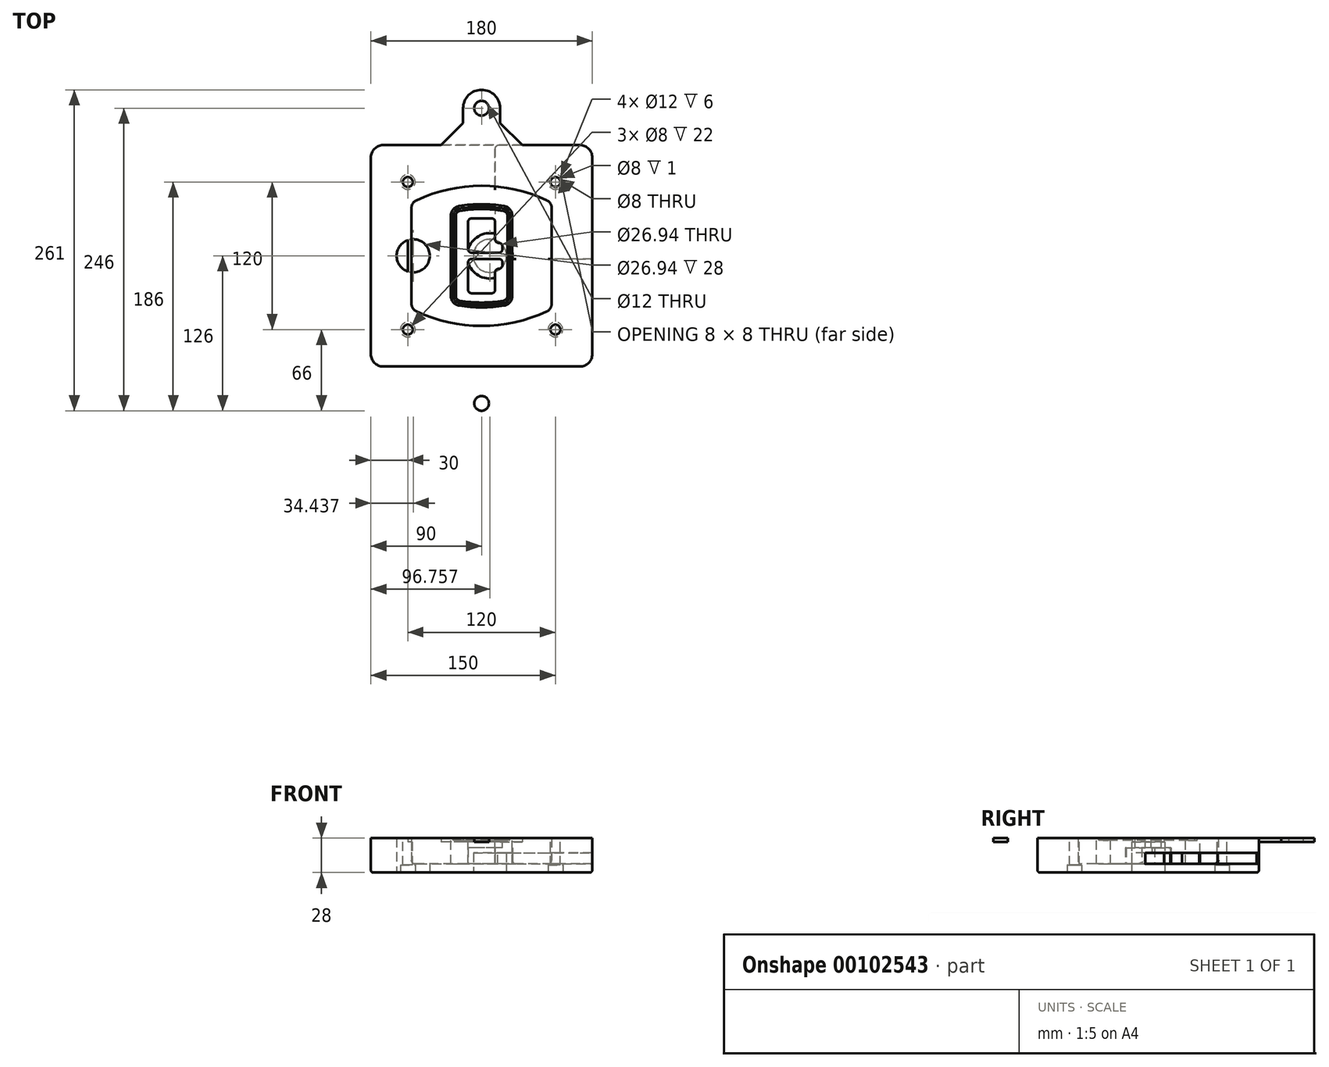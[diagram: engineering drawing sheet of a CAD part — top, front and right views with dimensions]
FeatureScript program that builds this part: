
annotation { "Feature Type Name" : "Feature", "Feature Type Description" : "" }
export const myFeature = defineFeature(function(context is Context, id is Id, definition is map)
    precondition{}
    {
        {
            var Q0;
            Q0=qCreatedBy(makeId("Top.planeOp"),FACE);
            var sketch = newSketch(context, id + "F0", { "sketchPlane" : qUnion([Q0])});
            skPoint(sketch, "E0.rect.middle", {"position": v(0, 0) * mm});
            skLineSegment(sketch, "E1.bottom", {"start": v(-80, -90) * mm, "end": v(80, -90) * mm});
            skLineSegment(sketch, "E1.top", {"start": v(-80, 90) * mm, "end": v(80, 90) * mm});
            skLineSegment(sketch, "E1.left", {"start": v(-90, -80) * mm, "end": v(-90, 80) * mm});
            skLineSegment(sketch, "E1.right", {"start": v(90, -80) * mm, "end": v(90, 80) * mm});
            skLineSegment(sketch, "E2", {"start": v(-90, 90) * mm, "end": v(90, -90) * mm, "construction": true});
            skLineSegment(sketch, "E3", {"start": v(90, 90) * mm, "end": v(-90, -90) * mm, "construction": true});
            skCircle(sketch, "E4", {"center": v(-60, 60) * mm, "radius": 4 * mm});
            skCircle(sketch, "E5", {"center": v(60, 60) * mm, "radius": 4 * mm});
            skCircle(sketch, "E6", {"center": v(60, -60) * mm, "radius": 4 * mm});
            skCircle(sketch, "E7", {"center": v(-60, -60) * mm, "radius": 4 * mm});
            skLineSegment(sketch, "E8", {"start": v(-60, 60) * mm, "end": v(60, 60) * mm, "construction": true});
            skLineSegment(sketch, "E9", {"start": v(60, 60) * mm, "end": v(60, -60) * mm, "construction": true});
            skLineSegment(sketch, "E10", {"start": v(60, -60) * mm, "end": v(-60, -60) * mm, "construction": true});
            skLineSegment(sketch, "E11", {"start": v(-60, -60) * mm, "end": v(-60, 60) * mm, "construction": true});
            skLineSegment(sketch, "E12", {"start": v(-60, 38.83) * mm, "end": v(-60, -38.83) * mm});
            skLineSegment(sketch, "E13", {"start": v(60, 38.83) * mm, "end": v(60, -38.83) * mm});
            skArc(sketch, "E14", {"start": v(54.26, 47.88) * mm, "mid": v(0, 60) * mm, "end": v(-54.26, 47.88) * mm});
            skArc(sketch, "E15", {"start": v(-54.26, -47.88) * mm, "mid": v(0, -60) * mm, "end": v(54.26, -47.88) * mm});
            skLineSegment(sketch, "E16", {"start": v(-60, 0) * mm, "end": v(60, 0) * mm, "construction": true});
            skPoint(sketch, "E17.visualSharp", {"position": v(-60, -45) * mm});
            skArc(sketch, "E17.filletArc", {"start": v(-60, -38.83) * mm, "mid": v(-58.44, -44.2) * mm, "end": v(-54.26, -47.88) * mm});
            skPoint(sketch, "E18.visualSharp", {"position": v(-60, 45) * mm});
            skArc(sketch, "E18.filletArc", {"start": v(-54.26, 47.88) * mm, "mid": v(-58.44, 44.2) * mm, "end": v(-60, 38.83) * mm});
            skPoint(sketch, "E19.visualSharp", {"position": v(60, 45) * mm});
            skArc(sketch, "E19.filletArc", {"start": v(60, 38.83) * mm, "mid": v(58.44, 44.2) * mm, "end": v(54.26, 47.88) * mm});
            skPoint(sketch, "E20.visualSharp", {"position": v(60, -45) * mm});
            skArc(sketch, "E20.filletArc", {"start": v(54.26, -47.88) * mm, "mid": v(58.44, -44.2) * mm, "end": v(60, -38.83) * mm});
            skPoint(sketch, "E21.visualSharp", {"position": v(-90, 90) * mm});
            skArc(sketch, "E21.filletArc", {"start": v(-80, 90) * mm, "mid": v(-87.07, 87.07) * mm, "end": v(-90, 80) * mm});
            skPoint(sketch, "E22.visualSharp", {"position": v(90, 90) * mm});
            skArc(sketch, "E22.filletArc", {"start": v(90, 80) * mm, "mid": v(87.07, 87.07) * mm, "end": v(80, 90) * mm});
            skPoint(sketch, "E23.visualSharp", {"position": v(90, -90) * mm});
            skArc(sketch, "E23.filletArc", {"start": v(80, -90) * mm, "mid": v(87.07, -87.07) * mm, "end": v(90, -80) * mm});
            skPoint(sketch, "E24.visualSharp", {"position": v(-90, -90) * mm});
            skArc(sketch, "E24.filletArc", {"start": v(-90, -80) * mm, "mid": v(-87.07, -87.07) * mm, "end": v(-80, -90) * mm});
            skArc(sketch, "E25.0", {"start": v(57, 38.83) * mm, "mid": v(55.9, 42.58) * mm, "end": v(52.98, 45.17) * mm});
            skLineSegment(sketch, "E25.1", {"start": v(57, 38.83) * mm, "end": v(57, -38.83) * mm});
            skArc(sketch, "E25.2", {"start": v(52.98, -45.17) * mm, "mid": v(55.9, -42.58) * mm, "end": v(57, -38.83) * mm});
            skArc(sketch, "E25.3", {"start": v(-52.98, -45.17) * mm, "mid": v(0, -57) * mm, "end": v(52.98, -45.17) * mm});
            skArc(sketch, "E25.4", {"start": v(-57, -38.83) * mm, "mid": v(-55.9, -42.58) * mm, "end": v(-52.98, -45.17) * mm});
            skArc(sketch, "E25.5", {"start": v(52.98, 45.17) * mm, "mid": v(0, 57) * mm, "end": v(-52.98, 45.17) * mm});
            skLineSegment(sketch, "E25.6", {"start": v(-57, 38.83) * mm, "end": v(-57, -38.83) * mm});
            skArc(sketch, "E25.7", {"start": v(-52.98, 45.17) * mm, "mid": v(-55.9, 42.58) * mm, "end": v(-57, 38.83) * mm});
            skArc(sketch, "E26.0", {"start": v(-55.96, 51.5) * mm, "mid": v(-61.82, 46.33) * mm, "end": v(-64, 38.83) * mm});
            skArc(sketch, "E26.1", {"start": v(55.96, 51.5) * mm, "mid": v(0, 64) * mm, "end": v(-55.96, 51.5) * mm});
            skArc(sketch, "E26.2", {"start": v(64, 38.83) * mm, "mid": v(61.82, 46.33) * mm, "end": v(55.96, 51.5) * mm});
            skLineSegment(sketch, "E26.3", {"start": v(64, 38.83) * mm, "end": v(64, -38.83) * mm});
            skArc(sketch, "E26.4", {"start": v(55.96, -51.5) * mm, "mid": v(61.82, -46.33) * mm, "end": v(64, -38.83) * mm});
            skLineSegment(sketch, "E26.5", {"start": v(-64, 38.83) * mm, "end": v(-64, -38.83) * mm});
            skArc(sketch, "E26.6", {"start": v(-55.96, -51.5) * mm, "mid": v(0, -64) * mm, "end": v(55.96, -51.5) * mm});
            skArc(sketch, "E26.7", {"start": v(-64, -38.83) * mm, "mid": v(-61.82, -46.33) * mm, "end": v(-55.96, -51.5) * mm});
            skSolve(sketch);
        }
        {
            var Q0;
            Q0=makeQuery(id+"F0.imprint","IMPRINT",FACE,{"disambiguationData":[TD([[makeQuery(id+"F0.imprint","IMPRINT",EDGE,{"derivedFrom":sQuery(id+"F0.wireOp",EDGE,"E1.bottom")}),1.0]])]});
            var Q1;
            Q1=makeQuery(id+"F0.imprint","IMPRINT",FACE,{"disambiguationData":[TD([[makeQuery(id+"F0.imprint","IMPRINT",EDGE,{"derivedFrom":sQuery(id+"F0.wireOp",EDGE,"E12")}),1.0]])]});
            var Q2;
            Q2=makeQuery(id+"F0.imprint","IMPRINT",FACE,{"disambiguationData":[TD([[makeQuery(id+"F0.imprint","IMPRINT",EDGE,{"derivedFrom":sQuery(id+"F0.wireOp",EDGE,"E25.0")}),1.0]])]});
            var Q3;
            Q3=makeQuery(id+"F0.imprint","IMPRINT",FACE,{"disambiguationData":[TD([[makeQuery(id+"F0.imprint","IMPRINT",EDGE,{"derivedFrom":sQuery(id+"F0.wireOp",EDGE,"E12")}),-1.0]])]});
            extrude(context, id + "F1", {"entities" : qUnion([Q0, Q1, Q2, Q3]), "oppositeDirection" : true, "depth" : 25 * mm});
        }
        {
            var Q0;
            Q0=makeQuery(id+"F0.imprint","IMPRINT",FACE,{"disambiguationData":[TD([[makeQuery(id+"F0.imprint","IMPRINT",EDGE,{"derivedFrom":sQuery(id+"F0.wireOp",EDGE,"E12")}),1.0]])]});
            extrude(context, id + "F2", {"entities" : qUnion([Q0]), "operationType" : NewBodyOperationType.ADD, "depth" : 3 * mm});
        }
        {
            var Q0;
            Q0=makeQuery(id+"F0.imprint","IMPRINT",FACE,{"disambiguationData":[TD([[makeQuery(id+"F0.imprint","IMPRINT",EDGE,{"derivedFrom":sQuery(id+"F0.wireOp",EDGE,"E25.0")}),1.0]])]});
            extrude(context, id + "F3", {"entities" : qUnion([Q0]), "operationType" : NewBodyOperationType.REMOVE, "oppositeDirection" : true, "depth" : 18 * mm});
        }
        {
            var Q0;
            Q0=makeQuery(id+"F2.opExtrude","CAP_FACE",FACE,{"disambiguationData":[OSD([sQuery(id+"F0.wireOp",EDGE,"E12"),sQuery(id+"F0.wireOp",EDGE,"E13"),sQuery(id+"F0.wireOp",EDGE,"E14"),sQuery(id+"F0.wireOp",EDGE,"E15"),sQuery(id+"F0.wireOp",EDGE,"E17.filletArc"),sQuery(id+"F0.wireOp",EDGE,"E18.filletArc"),sQuery(id+"F0.wireOp",EDGE,"E19.filletArc"),sQuery(id+"F0.wireOp",EDGE,"E20.filletArc"),sQuery(id+"F0.wireOp",EDGE,"E25.0"),sQuery(id+"F0.wireOp",EDGE,"E25.1"),sQuery(id+"F0.wireOp",EDGE,"E25.2"),sQuery(id+"F0.wireOp",EDGE,"E25.3"),sQuery(id+"F0.wireOp",EDGE,"E25.4"),sQuery(id+"F0.wireOp",EDGE,"E25.5"),sQuery(id+"F0.wireOp",EDGE,"E25.6"),sQuery(id+"F0.wireOp",EDGE,"E25.7")])],"isStart":false});
            var sketch = newSketch(context, id + "F4", { "sketchPlane" : qUnion([Q0])});
            skArc(sketch, "E27.0", {"start": v(-18.34, -40.45) * mm, "mid": v(0, -42) * mm, "end": v(18.34, -40.45) * mm});
            skArc(sketch, "E28.0", {"start": v(18.34, 40.45) * mm, "mid": v(0, 42) * mm, "end": v(-18.34, 40.45) * mm});
            skLineSegment(sketch, "E29", {"start": v(-25, 32.57) * mm, "end": v(-25, -32.57) * mm});
            skLineSegment(sketch, "E30", {"start": v(25, 32.57) * mm, "end": v(25, -32.57) * mm});
            skLineSegment(sketch, "E31", {"start": v(-25, 39.1) * mm, "end": v(25, 39.1) * mm, "construction": true});
            skLineSegment(sketch, "E32", {"start": v(-25, -39.1) * mm, "end": v(25, -39.1) * mm, "construction": true});
            skPoint(sketch, "E33.visualSharp", {"position": v(-25, 39.1) * mm});
            skArc(sketch, "E33.filletArc", {"start": v(-18.34, 40.45) * mm, "mid": v(-23.11, 37.73) * mm, "end": v(-25, 32.57) * mm});
            skPoint(sketch, "E34.visualSharp", {"position": v(25, 39.1) * mm});
            skArc(sketch, "E34.filletArc", {"start": v(25, 32.57) * mm, "mid": v(23.11, 37.73) * mm, "end": v(18.34, 40.45) * mm});
            skPoint(sketch, "E35.visualSharp", {"position": v(25, -39.1) * mm});
            skArc(sketch, "E35.filletArc", {"start": v(18.34, -40.45) * mm, "mid": v(23.11, -37.73) * mm, "end": v(25, -32.57) * mm});
            skPoint(sketch, "E36.visualSharp", {"position": v(-25, -39.1) * mm});
            skArc(sketch, "E36.filletArc", {"start": v(-25, -32.57) * mm, "mid": v(-23.11, -37.73) * mm, "end": v(-18.34, -40.45) * mm});
            skArc(sketch, "E37.0", {"start": v(52.98, 45.17) * mm, "mid": v(0, 57) * mm, "end": v(-52.98, 45.17) * mm});
            skArc(sketch, "E37.1", {"start": v(-52.98, 45.17) * mm, "mid": v(-55.9, 42.58) * mm, "end": v(-57, 38.83) * mm});
            skLineSegment(sketch, "E37.2", {"start": v(-57, 38.83) * mm, "end": v(-57, -38.83) * mm});
            skArc(sketch, "E37.3", {"start": v(-57, -38.83) * mm, "mid": v(-55.9, -42.58) * mm, "end": v(-52.98, -45.17) * mm});
            skArc(sketch, "E37.4", {"start": v(-52.98, -45.17) * mm, "mid": v(0, -57) * mm, "end": v(52.98, -45.17) * mm});
            skArc(sketch, "E37.5", {"start": v(52.98, -45.17) * mm, "mid": v(55.9, -42.58) * mm, "end": v(57, -38.83) * mm});
            skLineSegment(sketch, "E37.6", {"start": v(57, 38.83) * mm, "end": v(57, -38.83) * mm});
            skArc(sketch, "E37.7", {"start": v(57, 38.83) * mm, "mid": v(55.9, 42.58) * mm, "end": v(52.98, 45.17) * mm});
            skLineSegment(sketch, "E38.0", {"start": v(23, 32.57) * mm, "end": v(23, -32.57) * mm});
            skArc(sketch, "E38.1", {"start": v(18, -38.48) * mm, "mid": v(21.58, -36.44) * mm, "end": v(23, -32.57) * mm});
            skArc(sketch, "E38.2", {"start": v(-18, -38.48) * mm, "mid": v(0, -40) * mm, "end": v(18, -38.48) * mm});
            skArc(sketch, "E38.3", {"start": v(-23, -32.57) * mm, "mid": v(-21.58, -36.44) * mm, "end": v(-18, -38.48) * mm});
            skLineSegment(sketch, "E38.4", {"start": v(-23, 32.57) * mm, "end": v(-23, -32.57) * mm});
            skArc(sketch, "E38.5", {"start": v(23, 32.57) * mm, "mid": v(21.58, 36.44) * mm, "end": v(18, 38.48) * mm});
            skArc(sketch, "E38.6", {"start": v(-18, 38.48) * mm, "mid": v(-21.58, 36.44) * mm, "end": v(-23, 32.57) * mm});
            skArc(sketch, "E38.7", {"start": v(18, 38.48) * mm, "mid": v(0, 40) * mm, "end": v(-18, 38.48) * mm});
            skArc(sketch, "E39.0", {"start": v(21, 32.57) * mm, "mid": v(20.06, 35.15) * mm, "end": v(17.67, 36.5) * mm});
            skLineSegment(sketch, "E39.1", {"start": v(21, 32.57) * mm, "end": v(21, -32.57) * mm});
            skArc(sketch, "E39.2", {"start": v(17.67, -36.5) * mm, "mid": v(20.06, -35.15) * mm, "end": v(21, -32.57) * mm});
            skArc(sketch, "E39.3", {"start": v(-17.67, -36.5) * mm, "mid": v(0, -38) * mm, "end": v(17.67, -36.5) * mm});
            skArc(sketch, "E39.4", {"start": v(-21, -32.57) * mm, "mid": v(-20.06, -35.15) * mm, "end": v(-17.67, -36.5) * mm});
            skArc(sketch, "E39.5", {"start": v(17.67, 36.5) * mm, "mid": v(0, 38) * mm, "end": v(-17.67, 36.5) * mm});
            skLineSegment(sketch, "E39.6", {"start": v(-21, 32.57) * mm, "end": v(-21, -32.57) * mm});
            skArc(sketch, "E39.7", {"start": v(-17.67, 36.5) * mm, "mid": v(-20.06, 35.15) * mm, "end": v(-21, 32.57) * mm});
            skLineSegment(sketch, "E40", {"start": v(-25, 0) * mm, "end": v(25, 0) * mm, "construction": true});
            skLineSegment(sketch, "E41", {"start": v(-11, 5.5) * mm, "end": v(-11, 27.5) * mm});
            skLineSegment(sketch, "E42", {"start": v(-8, 30.5) * mm, "end": v(8, 30.5) * mm});
            skLineSegment(sketch, "E43", {"start": v(11, 27.5) * mm, "end": v(11, 13.5) * mm});
            skLineSegment(sketch, "E44", {"start": v(14, 10.5) * mm, "end": v(14, 10.5) * mm});
            skLineSegment(sketch, "E45", {"start": v(17, 7.5) * mm, "end": v(17, 5.5) * mm});
            skLineSegment(sketch, "E46", {"start": v(14, 2.5) * mm, "end": v(-8, 2.5) * mm});
            skPoint(sketch, "E47.visualSharp", {"position": v(-11, 30.5) * mm});
            skArc(sketch, "E47.filletArc", {"start": v(-8, 30.5) * mm, "mid": v(-10.12, 29.62) * mm, "end": v(-11, 27.5) * mm});
            skPoint(sketch, "E48.visualSharp", {"position": v(11, 30.5) * mm});
            skArc(sketch, "E48.filletArc", {"start": v(11, 27.5) * mm, "mid": v(10.12, 29.62) * mm, "end": v(8, 30.5) * mm});
            skPoint(sketch, "E49.visualSharp", {"position": v(11, 10.5) * mm});
            skArc(sketch, "E49.filletArc", {"start": v(11, 13.5) * mm, "mid": v(11.88, 11.38) * mm, "end": v(14, 10.5) * mm});
            skPoint(sketch, "E50.visualSharp", {"position": v(17, 10.5) * mm});
            skArc(sketch, "E50.filletArc", {"start": v(17, 7.5) * mm, "mid": v(16.12, 9.62) * mm, "end": v(14, 10.5) * mm});
            skPoint(sketch, "E51.visualSharp", {"position": v(17, 2.5) * mm});
            skArc(sketch, "E51.filletArc", {"start": v(14, 2.5) * mm, "mid": v(16.12, 3.38) * mm, "end": v(17, 5.5) * mm});
            skPoint(sketch, "E52.visualSharp", {"position": v(-11, 2.5) * mm});
            skArc(sketch, "E52.filletArc", {"start": v(-11, 5.5) * mm, "mid": v(-10.12, 3.38) * mm, "end": v(-8, 2.5) * mm});
            skLineSegment(sketch, "E53.0.MirrorCS", {"start": v(14, -2.5) * mm, "end": v(-8, -2.5) * mm});
            skArc(sketch, "E54.0.MirrorCS", {"start": v(-11, -5.5) * mm, "mid": v(-10.12, -3.38) * mm, "end": v(-8, -2.5) * mm});
            skLineSegment(sketch, "E55.0.MirrorCS", {"start": v(-11, -5.5) * mm, "end": v(-11, -27.5) * mm});
            skArc(sketch, "E56.0.MirrorCS", {"start": v(-8, -30.5) * mm, "mid": v(-10.12, -29.62) * mm, "end": v(-11, -27.5) * mm});
            skLineSegment(sketch, "E57.0.MirrorCS", {"start": v(-8, -30.5) * mm, "end": v(8, -30.5) * mm});
            skArc(sketch, "E58.0.MirrorCS", {"start": v(11, -27.5) * mm, "mid": v(10.12, -29.62) * mm, "end": v(8, -30.5) * mm});
            skLineSegment(sketch, "E59.0.MirrorCS", {"start": v(11, -27.5) * mm, "end": v(11, -13.5) * mm});
            skArc(sketch, "E60.0.MirrorCS", {"start": v(11, -13.5) * mm, "mid": v(11.88, -11.38) * mm, "end": v(14, -10.5) * mm});
            skArc(sketch, "E61.0.MirrorCS", {"start": v(17, -7.5) * mm, "mid": v(16.12, -9.62) * mm, "end": v(14, -10.5) * mm});
            skLineSegment(sketch, "E62.0.MirrorCS", {"start": v(17, -7.5) * mm, "end": v(17, -5.5) * mm});
            skArc(sketch, "E63.0.MirrorCS", {"start": v(14, -2.5) * mm, "mid": v(16.12, -3.38) * mm, "end": v(17, -5.5) * mm});
            skSolve(sketch);
        }
        {
            var Q0;
            Q0=makeQuery(id+"F4.imprint","IMPRINT",FACE,{"disambiguationData":[TD([[makeQuery(id+"F4.imprint","IMPRINT",EDGE,{"derivedFrom":sQuery(id+"F4.wireOp",EDGE,"E27.0")}),1.0]])]});
            var Q1;
            Q1=makeQuery(id+"F4.imprint","IMPRINT",FACE,{"disambiguationData":[TD([[makeQuery(id+"F4.imprint","IMPRINT",EDGE,{"derivedFrom":sQuery(id+"F4.wireOp",EDGE,"E38.0")}),-1.0]])]});
            var Q2;
            Q2=makeQuery(id+"F4.imprint","IMPRINT",FACE,{"disambiguationData":[TD([[makeQuery(id+"F4.imprint","IMPRINT",EDGE,{"derivedFrom":sQuery(id+"F4.wireOp",EDGE,"E39.0")}),1.0]])]});
            extrude(context, id + "F5", {"entities" : qUnion([Q0, Q1, Q2]), "operationType" : NewBodyOperationType.ADD, "endBound" : BoundingType.UP_TO_NEXT, "oppositeDirection" : true, "depth" : 25 * mm});
        }
        {
            var Q0;
            Q0=makeQuery(id+"F4.imprint","IMPRINT",FACE,{"disambiguationData":[TD([[makeQuery(id+"F4.imprint","IMPRINT",EDGE,{"derivedFrom":sQuery(id+"F4.wireOp",EDGE,"E38.0")}),-1.0]])]});
            extrude(context, id + "F6", {"entities" : qUnion([Q0]), "operationType" : NewBodyOperationType.REMOVE, "oppositeDirection" : true, "depth" : 2 * mm});
        }
        {
            var Q0;
            Q0=makeQuery(id+"F1.opExtrude","CAP_FACE",FACE,{"disambiguationData":[OSD([sQuery(id+"F0.wireOp",EDGE,"E1.bottom"),sQuery(id+"F0.wireOp",EDGE,"E1.top"),sQuery(id+"F0.wireOp",EDGE,"E1.left"),sQuery(id+"F0.wireOp",EDGE,"E1.right"),sQuery(id+"F0.wireOp",EDGE,"E4"),sQuery(id+"F0.wireOp",EDGE,"E5"),sQuery(id+"F0.wireOp",EDGE,"E6"),sQuery(id+"F0.wireOp",EDGE,"E7"),sQuery(id+"F0.wireOp",EDGE,"E21.filletArc"),sQuery(id+"F0.wireOp",EDGE,"E22.filletArc"),sQuery(id+"F0.wireOp",EDGE,"E23.filletArc"),sQuery(id+"F0.wireOp",EDGE,"E24.filletArc")])],"isStart":false});
            var sketch = newSketch(context, id + "F7", { "sketchPlane" : qUnion([Q0])});
            skCircle(sketch, "E64", {"center": v(6.76, 0) * mm, "radius": 13.47 * mm});
            skCircle(sketch, "E65", {"center": v(-55.56, 0) * mm, "radius": 13.47 * mm});
            skLineSegment(sketch, "E66", {"start": v(90, 0) * mm, "end": v(-90, 0) * mm});
            skCircle(sketch, "E67", {"center": v(6.76, 0) * mm, "radius": 18.47 * mm});
            skCircle(sketch, "E68", {"center": v(60, -60) * mm, "radius": 6 * mm});
            skCircle(sketch, "E69", {"center": v(-60, -60) * mm, "radius": 6 * mm});
            skCircle(sketch, "E70", {"center": v(-60, 60) * mm, "radius": 6 * mm});
            skCircle(sketch, "E71", {"center": v(60, 60) * mm, "radius": 6 * mm});
            skSolve(sketch);
        }
        {
            var Q0;
            {var subQ1=sQuery(id+"F7.wireOp",EDGE,"E66");var subQ4=sQuery(id+"F7.wireOp",EDGE,"E64");var subQ6=makeQuery(id+"F7.imprint","INTERSECT",VERTEX,{"disambiguationData":[OD(0.0)],"derivedFrom":[subQ4,subQ1]});Q0=makeQuery(id+"F7.imprint","IMPRINT",FACE,{"disambiguationData":[TD([[makeQuery(id+"F7.imprint","IMPRINT",EDGE,{"disambiguationData":[TD([[subQ6,-1.0]])],"derivedFrom":subQ4}),-1.0]])]});}
            var Q1;
            {var subQ0=sQuery(id+"F7.wireOp",EDGE,"E66");var subQ1=sQuery(id+"F7.wireOp",EDGE,"E64");var subQ3=makeQuery(id+"F7.imprint","INTERSECT",VERTEX,{"disambiguationData":[OD(0.0)],"derivedFrom":[subQ1,subQ0]});Q1=makeQuery(id+"F7.imprint","IMPRINT",FACE,{"disambiguationData":[TD([[makeQuery(id+"F7.imprint","IMPRINT",EDGE,{"disambiguationData":[TD([[subQ3,-1.0]])],"derivedFrom":subQ1}),1.0]])]});}
            var Q2;
            {var subQ0=sQuery(id+"F7.wireOp",EDGE,"E66");var subQ1=sQuery(id+"F7.wireOp",EDGE,"E64");var subQ3=makeQuery(id+"F7.imprint","INTERSECT",VERTEX,{"disambiguationData":[OD(0.0)],"derivedFrom":[subQ1,subQ0]});Q2=makeQuery(id+"F7.imprint","IMPRINT",FACE,{"disambiguationData":[TD([[makeQuery(id+"F7.imprint","IMPRINT",EDGE,{"disambiguationData":[TD([[subQ3,1.0]])],"derivedFrom":subQ1}),1.0]])]});}
            var Q3;
            {var subQ1=sQuery(id+"F7.wireOp",EDGE,"E66");var subQ4=sQuery(id+"F7.wireOp",EDGE,"E64");var subQ6=makeQuery(id+"F7.imprint","INTERSECT",VERTEX,{"disambiguationData":[OD(0.0)],"derivedFrom":[subQ4,subQ1]});Q3=makeQuery(id+"F7.imprint","IMPRINT",FACE,{"disambiguationData":[TD([[makeQuery(id+"F7.imprint","IMPRINT",EDGE,{"disambiguationData":[TD([[subQ6,1.0]])],"derivedFrom":subQ4}),-1.0]])]});}
            extrude(context, id + "F8", {"entities" : qUnion([Q0, Q1, Q2, Q3]), "operationType" : NewBodyOperationType.ADD, "oppositeDirection" : true, "depth" : 20 * mm});
        }
        {
            var Q0;
            {var subQ0=sQuery(id+"F7.wireOp",EDGE,"E66");var subQ1=sQuery(id+"F7.wireOp",EDGE,"E64");var subQ3=makeQuery(id+"F7.imprint","INTERSECT",VERTEX,{"disambiguationData":[OD(0.0)],"derivedFrom":[subQ1,subQ0]});Q0=makeQuery(id+"F7.imprint","IMPRINT",FACE,{"disambiguationData":[TD([[makeQuery(id+"F7.imprint","IMPRINT",EDGE,{"disambiguationData":[TD([[subQ3,-1.0]])],"derivedFrom":subQ1}),1.0]])]});}
            var Q1;
            {var subQ0=sQuery(id+"F7.wireOp",EDGE,"E66");var subQ1=sQuery(id+"F7.wireOp",EDGE,"E64");var subQ3=makeQuery(id+"F7.imprint","INTERSECT",VERTEX,{"disambiguationData":[OD(0.0)],"derivedFrom":[subQ1,subQ0]});Q1=makeQuery(id+"F7.imprint","IMPRINT",FACE,{"disambiguationData":[TD([[makeQuery(id+"F7.imprint","IMPRINT",EDGE,{"disambiguationData":[TD([[subQ3,1.0]])],"derivedFrom":subQ1}),1.0]])]});}
            extrude(context, id + "F9", {"entities" : qUnion([Q0, Q1]), "operationType" : NewBodyOperationType.REMOVE, "oppositeDirection" : true, "depth" : 16 * mm});
        }
        {
            var Q0;
            {var subQ0=sQuery(id+"F7.wireOp",EDGE,"E66");var subQ1=sQuery(id+"F7.wireOp",EDGE,"E65");var subQ3=makeQuery(id+"F7.imprint","INTERSECT",VERTEX,{"disambiguationData":[OD(0.0)],"derivedFrom":[subQ1,subQ0]});Q0=makeQuery(id+"F7.imprint","IMPRINT",FACE,{"disambiguationData":[TD([[makeQuery(id+"F7.imprint","IMPRINT",EDGE,{"disambiguationData":[TD([[subQ3,-1.0]])],"derivedFrom":subQ1}),1.0]])]});}
            var Q1;
            {var subQ0=sQuery(id+"F7.wireOp",EDGE,"E66");var subQ1=sQuery(id+"F7.wireOp",EDGE,"E65");var subQ3=makeQuery(id+"F7.imprint","INTERSECT",VERTEX,{"disambiguationData":[OD(0.0)],"derivedFrom":[subQ1,subQ0]});Q1=makeQuery(id+"F7.imprint","IMPRINT",FACE,{"disambiguationData":[TD([[makeQuery(id+"F7.imprint","IMPRINT",EDGE,{"disambiguationData":[TD([[subQ3,1.0]])],"derivedFrom":subQ1}),1.0]])]});}
            extrude(context, id + "F10", {"entities" : qUnion([Q0, Q1]), "operationType" : NewBodyOperationType.REMOVE, "oppositeDirection" : true, "depth" : 25 * mm});
        }
        {
            var Q0;
            Q0=makeQuery(id+"F7.imprint","IMPRINT",FACE,{"disambiguationData":[TD([[makeQuery(id+"F7.imprint","IMPRINT",EDGE,{"derivedFrom":sQuery(id+"F7.wireOp",EDGE,"E68")}),1.0]])]});
            var Q1;
            Q1=makeQuery(id+"F7.imprint","IMPRINT",FACE,{"disambiguationData":[TD([[makeQuery(id+"F7.imprint","IMPRINT",EDGE,{"derivedFrom":makeQuery(id+"F1.opExtrude","CAP_EDGE",EDGE,{"disambiguationData":[OSD([sQuery(id+"F0.wireOp",EDGE,"E5")])],"isStart":false})}),-1.0]])]});
            var Q2;
            Q2=makeQuery(id+"F7.imprint","IMPRINT",FACE,{"disambiguationData":[TD([[makeQuery(id+"F7.imprint","IMPRINT",EDGE,{"derivedFrom":sQuery(id+"F7.wireOp",EDGE,"E69")}),1.0]])]});
            var Q3;
            Q3=makeQuery(id+"F7.imprint","IMPRINT",FACE,{"disambiguationData":[TD([[makeQuery(id+"F7.imprint","IMPRINT",EDGE,{"derivedFrom":makeQuery(id+"F1.opExtrude","CAP_EDGE",EDGE,{"disambiguationData":[OSD([sQuery(id+"F0.wireOp",EDGE,"E4")])],"isStart":false})}),-1.0]])]});
            var Q4;
            Q4=makeQuery(id+"F7.imprint","IMPRINT",FACE,{"disambiguationData":[TD([[makeQuery(id+"F7.imprint","IMPRINT",EDGE,{"derivedFrom":sQuery(id+"F7.wireOp",EDGE,"E70")}),1.0]])]});
            var Q5;
            Q5=makeQuery(id+"F7.imprint","IMPRINT",FACE,{"disambiguationData":[TD([[makeQuery(id+"F7.imprint","IMPRINT",EDGE,{"derivedFrom":makeQuery(id+"F1.opExtrude","CAP_EDGE",EDGE,{"disambiguationData":[OSD([sQuery(id+"F0.wireOp",EDGE,"E7")])],"isStart":false})}),-1.0]])]});
            var Q6;
            Q6=makeQuery(id+"F7.imprint","IMPRINT",FACE,{"disambiguationData":[TD([[makeQuery(id+"F7.imprint","IMPRINT",EDGE,{"derivedFrom":sQuery(id+"F7.wireOp",EDGE,"E71")}),1.0]])]});
            var Q7;
            Q7=makeQuery(id+"F7.imprint","IMPRINT",FACE,{"disambiguationData":[TD([[makeQuery(id+"F7.imprint","IMPRINT",EDGE,{"derivedFrom":makeQuery(id+"F1.opExtrude","CAP_EDGE",EDGE,{"disambiguationData":[OSD([sQuery(id+"F0.wireOp",EDGE,"E6")])],"isStart":false})}),-1.0]])]});
            extrude(context, id + "F11", {"entities" : qUnion([Q0, Q1, Q2, Q3, Q4, Q5, Q6, Q7]), "operationType" : NewBodyOperationType.REMOVE, "oppositeDirection" : true, "depth" : 6 * mm});
        }
        {
            var Q0;
            Q0=makeQuery(id+"F9.boolean.opBoolean","COPY",FACE,{"derivedFrom":makeQuery(id+"F9.opExtrude","CAP_FACE",FACE,{"disambiguationData":[OSD([sQuery(id+"F7.wireOp",EDGE,"E64")])],"isStart":false})});
            var sketch = newSketch(context, id + "F12", { "sketchPlane" : qUnion([Q0])});
            skArc(sketch, "E72.0", {"start": v(11, -88.19) * mm, "mid": v(97.1, -83.6) * mm, "end": v(92.5, 2.5) * mm});
            skLineSegment(sketch, "E72.1", {"start": v(11, -17.97) * mm, "end": v(11, -17.97) * mm});
            skLineSegment(sketch, "E73.0", {"start": v(92.5, 2.5) * mm, "end": v(14, 2.5) * mm});
            skArc(sketch, "E73.1", {"start": v(14, 2.5) * mm, "mid": v(16.12, 3.38) * mm, "end": v(17, 5.5) * mm});
            skLineSegment(sketch, "E73.2", {"start": v(17, 7.5) * mm, "end": v(17, 5.5) * mm});
            skArc(sketch, "E73.3", {"start": v(17, 7.5) * mm, "mid": v(16.12, 9.62) * mm, "end": v(14, 10.5) * mm});
            skArc(sketch, "E73.4", {"start": v(11, 13.5) * mm, "mid": v(11.88, 11.38) * mm, "end": v(14, 10.5) * mm});
            skLineSegment(sketch, "E73.5", {"start": v(11, 13.5) * mm, "end": v(11, -88.19) * mm});
            skLineSegment(sketch, "E73.7", {"start": v(92.5, -2.5) * mm, "end": v(14, -2.5) * mm});
            skArc(sketch, "E73.8", {"start": v(14, -2.5) * mm, "mid": v(16.12, -3.38) * mm, "end": v(17, -5.5) * mm});
            skLineSegment(sketch, "E73.9", {"start": v(17, -7.5) * mm, "end": v(17, -5.5) * mm});
            skArc(sketch, "E73.10", {"start": v(17, -7.5) * mm, "mid": v(16.12, -9.62) * mm, "end": v(14, -10.5) * mm});
            skArc(sketch, "E73.11", {"start": v(11, -13.5) * mm, "mid": v(11.88, -11.38) * mm, "end": v(14, -10.5) * mm});
            skLineSegment(sketch, "E73.12", {"start": v(11, -17.97) * mm, "end": v(11, -13.5) * mm});
            skPoint(sketch, "E74.orphan", {"position": v(11, -27.5) * mm});
            skPoint(sketch, "E75.orphan", {"position": v(-8, -2.5) * mm});
            skPoint(sketch, "E76.orphan", {"position": v(-8, 2.5) * mm});
            skPoint(sketch, "E77.orphan", {"position": v(11, 27.5) * mm});
            skSolve(sketch);
        }
        {
            var Q0;
            {var subQ7=sQuery(id+"F12.wireOp",EDGE,"E72.0");var subQ14=sQuery(id+"F12.wireOp",EDGE,"E72.1");var subQ16=sQuery(id+"F12.wireOp",EDGE,"E73.1");var subQ18=sQuery(id+"F12.wireOp",EDGE,"E73.8");Q0=qUnion([makeQuery(id+"F12.imprint","IMPRINT",FACE,{"disambiguationData":[TD([[makeQuery(id+"F12.imprint","IMPRINT",EDGE,{"derivedFrom":subQ7}),1.0]])]}),makeQuery(id+"F12.imprint","IMPRINT",FACE,{"disambiguationData":[TD([[makeQuery(id+"F12.imprint","IMPRINT",EDGE,{"derivedFrom":subQ14}),1.0]])]}),makeQuery(id+"F12.imprint","IMPRINT",FACE,{"disambiguationData":[TD([[makeQuery(id+"F12.imprint","IMPRINT",EDGE,{"derivedFrom":subQ16}),1.0]])]}),makeQuery(id+"F12.imprint","IMPRINT",FACE,{"disambiguationData":[TD([[makeQuery(id+"F12.imprint","IMPRINT",EDGE,{"derivedFrom":subQ18}),-1.0]])]})]);}
            var Q1;
            Q1=makeQuery(id+"F5.boolean.opBoolean","SPLIT",FACE,{"disambiguationData":[TD([makeQuery(id+"F5.opExtrude","SWEPT_FACE",FACE,{"disambiguationData":[OSD([sQuery(id+"F4.wireOp",EDGE,"E41")])]})])],"derivedFrom":makeQuery(id+"F3.boolean.opBoolean","COPY",FACE,{"derivedFrom":makeQuery(id+"F3.opExtrude","CAP_FACE",FACE,{"disambiguationData":[OSD([sQuery(id+"F0.wireOp",EDGE,"E25.0"),sQuery(id+"F0.wireOp",EDGE,"E25.1"),sQuery(id+"F0.wireOp",EDGE,"E25.2"),sQuery(id+"F0.wireOp",EDGE,"E25.3"),sQuery(id+"F0.wireOp",EDGE,"E25.4"),sQuery(id+"F0.wireOp",EDGE,"E25.5"),sQuery(id+"F0.wireOp",EDGE,"E25.6"),sQuery(id+"F0.wireOp",EDGE,"E25.7")])],"isStart":false})})});
            extrude(context, id + "F13", {"entities" : qUnion([Q0]), "operationType" : NewBodyOperationType.REMOVE, "endBound" : BoundingType.UP_TO_SURFACE, "endBoundEntityFace" : qUnion([Q1]), "depth" : 25 * mm});
        }
        {
            var Q0;
            Q0=makeQuery(id+"F3.boolean.opBoolean","COPY",EDGE,{"derivedFrom":makeQuery(id+"F3.opExtrude","CAP_EDGE",EDGE,{"disambiguationData":[OSD([sQuery(id+"F0.wireOp",EDGE,"E25.6")])],"isStart":false})});
            var Q1;
            Q1=makeQuery(id+"F8.boolean.opBoolean","INTERSECT",EDGE,{"derivedFrom":[makeQuery(id+"F5.opExtrude","SWEPT_FACE",FACE,{"disambiguationData":[OSD([sQuery(id+"F4.wireOp",EDGE,"E30")])]}),makeQuery(id+"F8.opExtrude","CAP_FACE",FACE,{"disambiguationData":[OSD([sQuery(id+"F7.wireOp",EDGE,"E67")])],"isStart":false})]});
            var Q2;
            Q2=makeQuery(id+"F8.boolean.opBoolean","INTERSECT",EDGE,{"disambiguationData":[OD(1.0)],"derivedFrom":[makeQuery(id+"F5.opExtrude","SWEPT_FACE",FACE,{"disambiguationData":[OSD([sQuery(id+"F4.wireOp",EDGE,"E30")])]}),makeQuery(id+"F8.opExtrude","SWEPT_FACE",FACE,{"disambiguationData":[OSD([sQuery(id+"F7.wireOp",EDGE,"E67")])]})]});
            var Q3;
            {var subQ0=makeQuery(id+"F3.boolean.opBoolean","COPY",FACE,{"derivedFrom":makeQuery(id+"F3.opExtrude","CAP_FACE",FACE,{"disambiguationData":[OSD([sQuery(id+"F0.wireOp",EDGE,"E25.0"),sQuery(id+"F0.wireOp",EDGE,"E25.1"),sQuery(id+"F0.wireOp",EDGE,"E25.2"),sQuery(id+"F0.wireOp",EDGE,"E25.3"),sQuery(id+"F0.wireOp",EDGE,"E25.4"),sQuery(id+"F0.wireOp",EDGE,"E25.5"),sQuery(id+"F0.wireOp",EDGE,"E25.6"),sQuery(id+"F0.wireOp",EDGE,"E25.7")])],"isStart":false})});var subQ1=sQuery(id+"F4.wireOp",EDGE,"E30");Q3=makeQuery(id+"F8.boolean.opBoolean","SPLIT",EDGE,{"disambiguationData":[TD([makeQuery(id+"F5.opExtrude","SWEPT_FACE",FACE,{"disambiguationData":[OSD([sQuery(id+"F4.wireOp",EDGE,"E35.filletArc")])]})])],"derivedFrom":makeQuery(id+"F5.opExtrude","TWEAK_EDGE",EDGE,{"derivedFrom":[subQ0,makeQuery(id+"F4.imprint","IMPRINT",EDGE,{"derivedFrom":subQ1})]})});}
            var Q4;
            {var subQ0=sQuery(id+"F0.wireOp",EDGE,"E25.0");var subQ1=sQuery(id+"F0.wireOp",EDGE,"E25.1");var subQ2=sQuery(id+"F0.wireOp",EDGE,"E25.2");var subQ3=sQuery(id+"F0.wireOp",EDGE,"E25.3");var subQ4=sQuery(id+"F0.wireOp",EDGE,"E25.4");var subQ5=sQuery(id+"F0.wireOp",EDGE,"E25.5");var subQ6=sQuery(id+"F0.wireOp",EDGE,"E25.6");var subQ7=sQuery(id+"F0.wireOp",EDGE,"E25.7");Q4=makeQuery(id+"F8.boolean.opBoolean","INTERSECT",EDGE,{"derivedFrom":[makeQuery(id+"F5.boolean.opBoolean","SPLIT",FACE,{"disambiguationData":[TD([makeQuery(id+"F2.opExtrude","SWEPT_FACE",FACE,{"disambiguationData":[OSD([subQ0])]})])],"derivedFrom":makeQuery(id+"F3.boolean.opBoolean","COPY",FACE,{"derivedFrom":makeQuery(id+"F3.opExtrude","CAP_FACE",FACE,{"disambiguationData":[OSD([subQ0,subQ1,subQ2,subQ3,subQ4,subQ5,subQ6,subQ7])],"isStart":false})})}),makeQuery(id+"F8.opExtrude","SWEPT_FACE",FACE,{"disambiguationData":[OSD([sQuery(id+"F7.wireOp",EDGE,"E67")])]})]});}
            var Q5;
            Q5=makeQuery(id+"F8.boolean.opBoolean","INTERSECT",EDGE,{"disambiguationData":[OD(0.0)],"derivedFrom":[makeQuery(id+"F5.opExtrude","SWEPT_FACE",FACE,{"disambiguationData":[OSD([sQuery(id+"F4.wireOp",EDGE,"E30")])]}),makeQuery(id+"F8.opExtrude","SWEPT_FACE",FACE,{"disambiguationData":[OSD([sQuery(id+"F7.wireOp",EDGE,"E67")])]})]});
            fillet(context, id + "F14", {"entities" : qUnion([Q0, Q1, Q2, Q3, Q4, Q5]), "radius" : 3 * mm, "tangentPropagation" : true, "allowEdgeOverflow" : false});
        }
        {
            var Q0;
            Q0=makeQuery(id+"F1.opExtrude","CAP_EDGE",EDGE,{"disambiguationData":[OSD([sQuery(id+"F0.wireOp",EDGE,"E1.bottom")])],"isStart":false});
            fillet(context, id + "F15", {"entities" : qUnion([Q0]), "radius" : 2 * mm, "tangentPropagation" : true, "allowEdgeOverflow" : false});
        }
        {
            var Q0;
            {var subQ0=sQuery(id+"F0.wireOp",EDGE,"E22.filletArc");var subQ1=sQuery(id+"F0.wireOp",EDGE,"E7");var subQ2=sQuery(id+"F0.wireOp",EDGE,"E6");var subQ3=sQuery(id+"F0.wireOp",EDGE,"E5");var subQ4=sQuery(id+"F0.wireOp",EDGE,"E4");var subQ5=sQuery(id+"F0.wireOp",EDGE,"E1.bottom");var subQ6=sQuery(id+"F0.wireOp",EDGE,"E21.filletArc");var subQ7=sQuery(id+"F0.wireOp",EDGE,"E1.top");var subQ8=sQuery(id+"F0.wireOp",EDGE,"E1.left");var subQ9=sQuery(id+"F0.wireOp",EDGE,"E1.right");var subQ10=sQuery(id+"F0.wireOp",EDGE,"E23.filletArc");var subQ11=sQuery(id+"F0.wireOp",EDGE,"E24.filletArc");Q0=makeQuery(id+"F2.boolean.opBoolean","SPLIT",FACE,{"disambiguationData":[TD([makeQuery(id+"F1.opExtrude","SWEPT_FACE",FACE,{"disambiguationData":[OSD([subQ5])]})])],"derivedFrom":makeQuery(id+"F1.opExtrude","CAP_FACE",FACE,{"disambiguationData":[OSD([subQ5,subQ7,subQ8,subQ9,subQ4,subQ3,subQ2,subQ1,subQ6,subQ0,subQ10,subQ11])],"isStart":true})});}
            var sketch = newSketch(context, id + "F16", { "sketchPlane" : qUnion([Q0])});
            skLineSegment(sketch, "E78", {"start": v(0, 90) * mm, "end": v(0, 120) * mm, "construction": true});
            skLineSegment(sketch, "E79", {"start": v(-15, 108) * mm, "end": v(-15, 120) * mm});
            skCircle(sketch, "E80", {"center": v(0, 120) * mm, "radius": 6 * mm});
            skArc(sketch, "E81", {"start": v(15, 120) * mm, "mid": v(0, 135) * mm, "end": v(-15, 120) * mm});
            skLineSegment(sketch, "E82", {"start": v(-90, 0) * mm, "end": v(90, 0) * mm, "construction": true});
            skLineSegment(sketch, "E83.MirrorCS", {"start": v(-15, -108) * mm, "end": v(-15, -120) * mm});
            skLineSegment(sketch, "E84.MirrorCS", {"start": v(0, -90) * mm, "end": v(0, -120) * mm, "construction": true});
            skCircle(sketch, "E85.MirrorC", {"center": v(0, -120) * mm, "radius": 6 * mm});
            skArc(sketch, "E86.MirrorCS", {"start": v(15, -120) * mm, "mid": v(0, -135) * mm, "end": v(-15, -120) * mm});
            skLineSegment(sketch, "E87", {"start": v(-15, 108) * mm, "end": v(-33, 90) * mm});
            skLineSegment(sketch, "E88", {"start": v(-33, 90) * mm, "end": v(-27.15, 95.85) * mm});
            skLineSegment(sketch, "E89", {"start": v(15, 120) * mm, "end": v(15, 108) * mm});
            skLineSegment(sketch, "E90", {"start": v(15, 108) * mm, "end": v(33, 90) * mm});
            skLineSegment(sketch, "E91.MirrorCS", {"start": v(-15, -108) * mm, "end": v(-33, -90) * mm});
            skLineSegment(sketch, "E92.MirrorCS", {"start": v(15, -120) * mm, "end": v(15, -108) * mm});
            skLineSegment(sketch, "E93.MirrorCS", {"start": v(15, -108) * mm, "end": v(33, -90) * mm});
            skSolve(sketch);
        }
        {
            var Q0;
            Q0=makeQuery(id+"F16.imprint","IMPRINT",FACE,{"disambiguationData":[TD([[makeQuery(id+"F16.imprint","IMPRINT",EDGE,{"derivedFrom":sQuery(id+"F16.wireOp",EDGE,"E85.MirrorC")}),1.0]])]});
            var Q1;
            Q1=makeQuery(id+"F16.imprint","IMPRINT",FACE,{"disambiguationData":[TD([[makeQuery(id+"F16.imprint","IMPRINT",EDGE,{"derivedFrom":sQuery(id+"F16.wireOp",EDGE,"E79")}),-1.0]])]});
            var Q2;
            {var subQ18=sQuery(id+"F0.wireOp",EDGE,"E1.left");Q2=makeQuery(id+"F16.imprint","IMPRINT",FACE,{"disambiguationData":[TD([[makeQuery(id+"F16.imprint","IMPRINT",EDGE,{"derivedFrom":makeQuery(id+"F1.opExtrude","CAP_EDGE",EDGE,{"disambiguationData":[OSD([subQ18])],"isStart":true})}),-1.0]])]});}
            var Q3;
            {var subQ0=sQuery(id+"F4.wireOp",EDGE,"E29");var subQ1=sQuery(id+"F4.wireOp",EDGE,"E35.filletArc");var subQ2=sQuery(id+"F4.wireOp",EDGE,"E34.filletArc");var subQ3=sQuery(id+"F4.wireOp",EDGE,"E36.filletArc");var subQ4=sQuery(id+"F4.wireOp",EDGE,"E33.filletArc");var subQ5=sQuery(id+"F4.wireOp",EDGE,"E30");var subQ6=sQuery(id+"F4.wireOp",EDGE,"E27.0");var subQ7=sQuery(id+"F4.wireOp",EDGE,"E28.0");Q3=makeQuery(id+"F6.boolean.opBoolean","SPLIT",FACE,{"disambiguationData":[TD([makeQuery(id+"F5.opExtrude","SWEPT_FACE",FACE,{"disambiguationData":[OSD([subQ6])]})])],"derivedFrom":makeQuery(id+"F5.opExtrude","CAP_FACE",FACE,{"disambiguationData":[OSD([subQ6,subQ7,subQ0,subQ5,subQ4,subQ2,subQ1,subQ3,sQuery(id+"F4.wireOp",EDGE,"E41"),sQuery(id+"F4.wireOp",EDGE,"E42"),sQuery(id+"F4.wireOp",EDGE,"E43"),sQuery(id+"F4.wireOp",EDGE,"E45"),sQuery(id+"F4.wireOp",EDGE,"E46"),sQuery(id+"F4.wireOp",EDGE,"E47.filletArc"),sQuery(id+"F4.wireOp",EDGE,"E48.filletArc"),sQuery(id+"F4.wireOp",EDGE,"E49.filletArc"),sQuery(id+"F4.wireOp",EDGE,"E50.filletArc"),sQuery(id+"F4.wireOp",EDGE,"E51.filletArc"),sQuery(id+"F4.wireOp",EDGE,"E52.filletArc"),sQuery(id+"F4.wireOp",EDGE,"E53.0.MirrorCS"),sQuery(id+"F4.wireOp",EDGE,"E54.0.MirrorCS"),sQuery(id+"F4.wireOp",EDGE,"E55.0.MirrorCS"),sQuery(id+"F4.wireOp",EDGE,"E56.0.MirrorCS"),sQuery(id+"F4.wireOp",EDGE,"E57.0.MirrorCS"),sQuery(id+"F4.wireOp",EDGE,"E58.0.MirrorCS"),sQuery(id+"F4.wireOp",EDGE,"E59.0.MirrorCS"),sQuery(id+"F4.wireOp",EDGE,"E60.0.MirrorCS"),sQuery(id+"F4.wireOp",EDGE,"E61.0.MirrorCS"),sQuery(id+"F4.wireOp",EDGE,"E62.0.MirrorCS"),sQuery(id+"F4.wireOp",EDGE,"E63.0.MirrorCS")])],"isStart":true})});}
            extrude(context, id + "F17", {"entities" : qUnion([Q0, Q1, Q2]), "operationType" : NewBodyOperationType.ADD, "endBound" : BoundingType.UP_TO_SURFACE, "endBoundEntityFace" : qUnion([Q3]), "depth" : 25 * mm});
        }
    });
